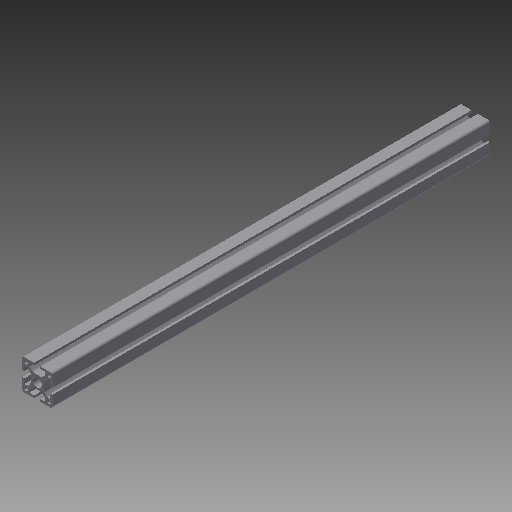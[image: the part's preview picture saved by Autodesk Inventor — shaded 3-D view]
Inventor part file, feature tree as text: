
AUTODESK INVENTOR PART (.ipt)
format: ipt  version: 2018 (Build 220112000, 112)  size: 221,696 bytes
history: native  units: mm
features: other x42, sketch x5, hole x4, extrude x1
ambient origin geometry x8: Origin, YZ Plane, XZ Plane, XY Plane, X Axis, Y Axis, Z Axis, Center Point
bodies: Solid1 (feature_tree)
feature tree (52):
  extrude  "Extrusion1"  [1 undecoded]
  hole  "Drilling 1"  [1 undecoded]
  hole  "Drilling 2"  [1 undecoded]
  hole  "Drilling 3"  [1 undecoded]
  hole  "Drilling 4"  [1 undecoded]
  other  "side_4d_XY"
  other  "side_4d_YZ"
  other  "side_4d_ZX"
  other  "side_4d_X"
  other  "side_4d_Y"
  other  "side_4d_Z"
  other  "side_4d_Center"
  other  "side_1a_XY"
  other  "side_1a_YZ"
  other  "side_1a_ZX"
  other  "side_1a_X"
  other  "side_1a_Y"
  other  "side_1a_Z"
  other  "side_1a_Center"
  other  "side_2b_XY"
  other  "side_2b_YZ"
  other  "side_2b_ZX"
  other  "side_2b_X"
  other  "side_2b_Y"
  other  "side_2b_Z"
  other  "side_2b_Center"
  other  "side_3c_XY"
  other  "side_3c_YZ"
  other  "side_3c_ZX"
  other  "side_3c_X"
  other  "side_3c_Y"
  other  "side_3c_Z"
  other  "side_3c_Center"
  other  "end_XY"
  other  "end_YZ"
  other  "end_ZX"
  other  "end_X"
  other  "end_Y"
  other  "end_Z"
  other  "end_Center"
  other  "start_XY"
  other  "start_YZ"
  other  "start_ZX"
  other  "start_X"
  other  "start_Y"
  other  "start_Z"
  other  "start_Center"
  sketch  "Skizze_1"  dims[d0=572.0mm d1=0.0mm]
  sketch  "Sketch2"  dims[d2=5.0mm d3=6.0mm d4=4.0mm d5=2.0mm d6=90.0deg d7=6000.0mm d8=0.0mm]
  sketch  "Sketch3"  dims[d9=5.0mm d10=6.0mm d11=4.0mm d12=2.0mm d13=90.0deg d14=6000.0mm d15=0.0mm]
  sketch  "Sketch4"  dims[d16=5.0mm d17=6.0mm d18=4.0mm d19=2.0mm d20=90.0deg d21=6000.0mm d22=0.0mm]
  sketch  "Sketch5"  dims[d23=5.0mm d24=6.0mm d25=4.0mm d26=2.0mm d27=90.0deg d28=6000.0mm d29=0.0mm]
note: 5 required parameter values undecoded (feature->parameter linkage not recoverable at this tier; creation-order binding heuristic only, values carry confidence <= 0.55)
